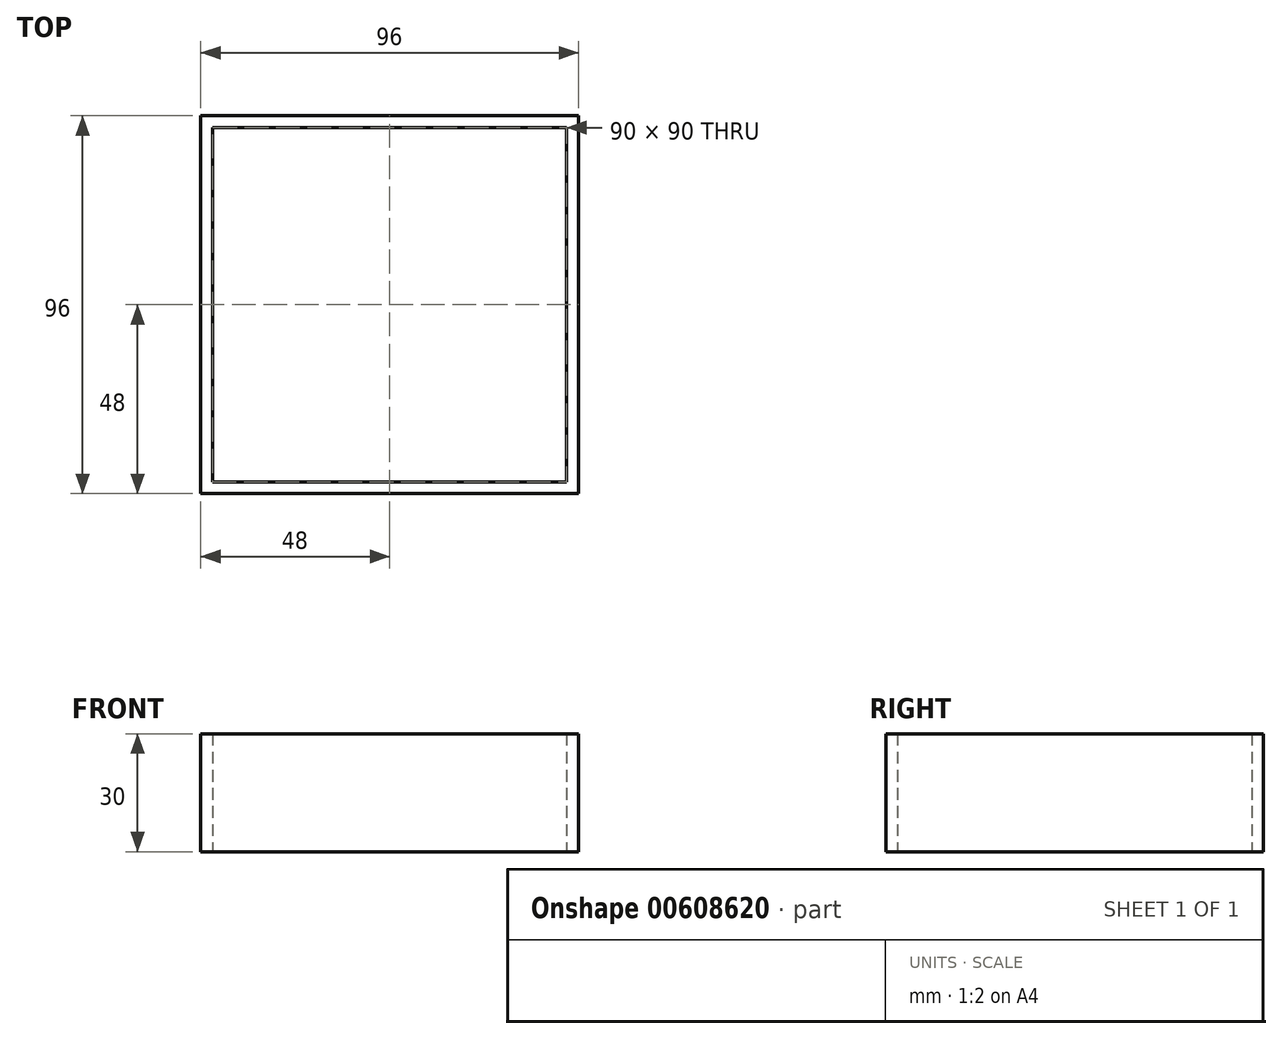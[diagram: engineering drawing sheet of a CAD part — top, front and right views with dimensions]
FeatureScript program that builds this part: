
annotation { "Feature Type Name" : "Feature", "Feature Type Description" : "" }
export const myFeature = defineFeature(function(context is Context, id is Id, definition is map)
    precondition{}
    {
        {
            var Q0;
            Q0=qCreatedBy(makeId("Top.planeOp"),FACE);
            var sketch = newSketch(context, id + "F0", { "sketchPlane" : qUnion([Q0])});
            skLineSegment(sketch, "E0.bottom", {"start": v(45, 45) * mm, "end": v(-45, 45) * mm});
            skLineSegment(sketch, "E0.top", {"start": v(45, -45) * mm, "end": v(-45, -45) * mm});
            skLineSegment(sketch, "E0.left", {"start": v(45, 45) * mm, "end": v(45, -45) * mm});
            skLineSegment(sketch, "E0.right", {"start": v(-45, 45) * mm, "end": v(-45, -45) * mm});
            skPoint(sketch, "E0.middle", {"position": v(0, 0) * mm});
            skLineSegment(sketch, "E1.bottom", {"start": v(-48, 48) * mm, "end": v(48, 48) * mm});
            skLineSegment(sketch, "E1.top", {"start": v(-48, -48) * mm, "end": v(48, -48) * mm});
            skLineSegment(sketch, "E1.left", {"start": v(-48, 48) * mm, "end": v(-48, -48) * mm});
            skLineSegment(sketch, "E1.right", {"start": v(48, 48) * mm, "end": v(48, -48) * mm});
            skSolve(sketch);
        }
        {
            var Q0;
            Q0=makeQuery(id+"F0.imprint","IMPRINT",FACE,{"disambiguationData":[TD([[makeQuery(id+"F0.imprint","IMPRINT",EDGE,{"derivedFrom":sQuery(id+"F0.wireOp",EDGE,"E0.bottom")}),-1.0]])]});
            extrude(context, id + "F1", {"entities" : qUnion([Q0]), "depth" : 30 * mm, "offsetDistance" : 25 * mm});
        }
    });
